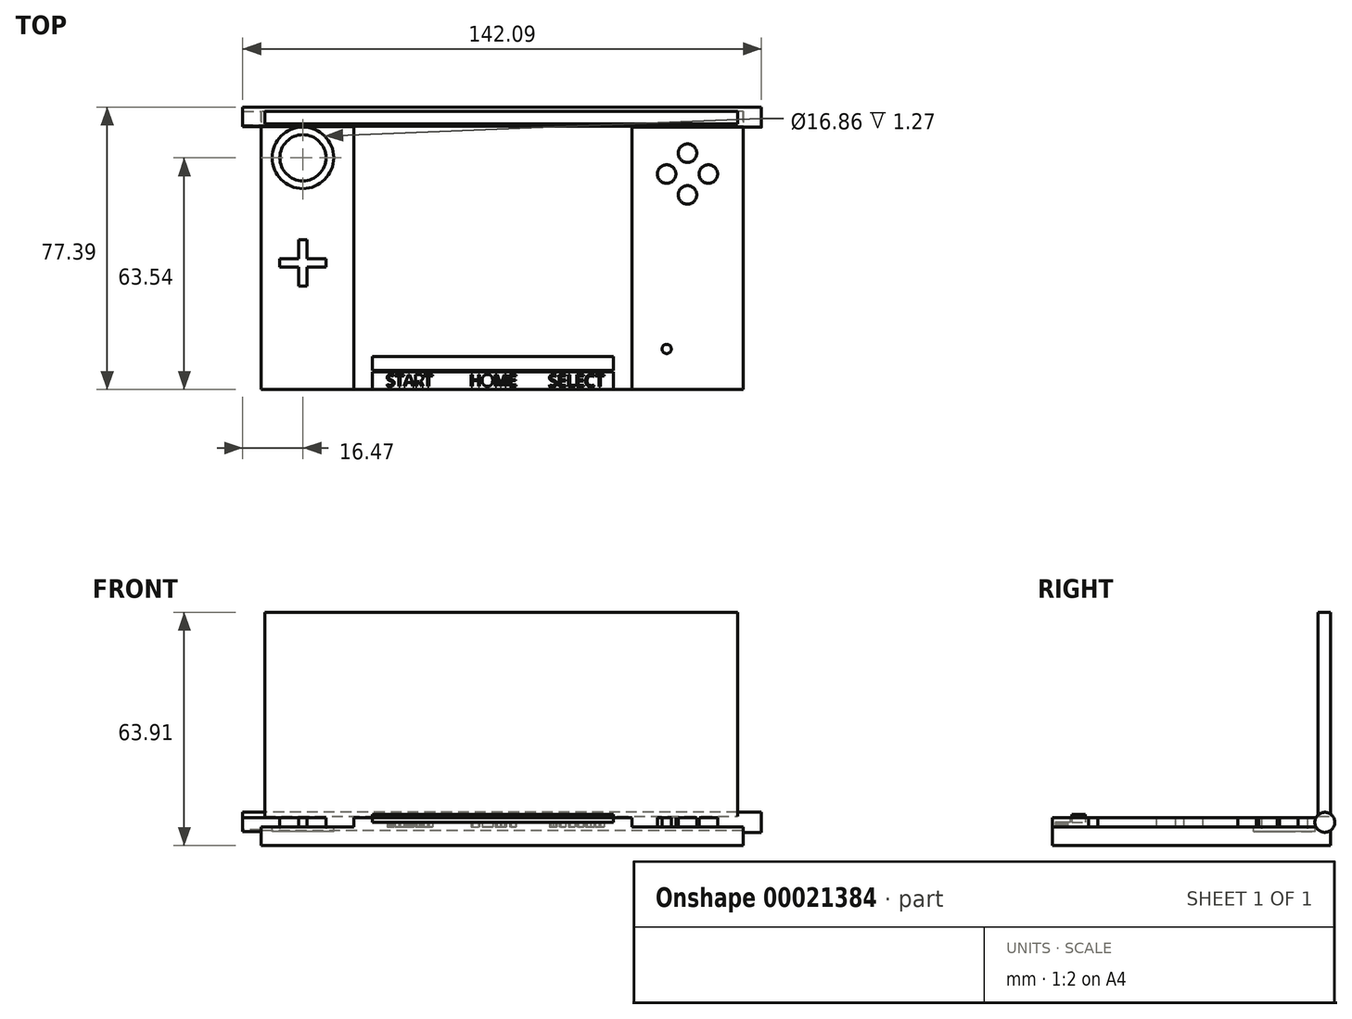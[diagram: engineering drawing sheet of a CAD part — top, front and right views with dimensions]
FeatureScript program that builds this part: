
annotation { "Feature Type Name" : "Feature", "Feature Type Description" : "" }
export const myFeature = defineFeature(function(context is Context, id is Id, definition is map)
    precondition{}
    {
        {
            var Q0;
            Q0=qCreatedBy(makeId("Front.planeOp"),FACE);
            var sketch = newSketch(context, id + "F0", { "sketchPlane" : qUnion([Q0])});
            skLineSegment(sketch, "E0.rect.bottom", {"start": v(-66.04, -2.54) * mm, "end": v(66.04, -2.54) * mm});
            skLineSegment(sketch, "E0.rect.top", {"start": v(-66.04, 2.54) * mm, "end": v(66.04, 2.54) * mm});
            skLineSegment(sketch, "E0.rect.left", {"start": v(-66.04, -2.54) * mm, "end": v(-66.04, 2.54) * mm});
            skLineSegment(sketch, "E0.rect.right", {"start": v(66.04, -2.54) * mm, "end": v(66.04, 2.54) * mm});
            skPoint(sketch, "E0.rect.middle", {"position": v(0, 0) * mm});
            skSolve(sketch);
        }
        {
            var Q0;
            Q0=makeQuery(id+"F0.imprint","IMPRINT",FACE,{"disambiguationData":[TD([[makeQuery(id+"F0.imprint","IMPRINT",EDGE,{"derivedFrom":sQuery(id+"F0.wireOp",EDGE,"E0.rect.bottom")}),1.0]])]});
            extrude(context, id + "F1", {"entities" : qUnion([Q0]), "depth" : 76.2 * mm});
        }
        {
            var Q0;
            Q0=makeQuery(id+"F1.opExtrude","SWEPT_FACE",FACE,{"disambiguationData":[OSD([sQuery(id+"F0.wireOp",EDGE,"E0.rect.top")])]});
            var sketch = newSketch(context, id + "F2", { "sketchPlane" : qUnion([Q0])});
            skLineSegment(sketch, "E1.bottom", {"start": v(-40.64, 0) * mm, "end": v(35.56, 0) * mm});
            skLineSegment(sketch, "E1.top", {"start": v(-40.64, -76.2) * mm, "end": v(35.56, -76.2) * mm});
            skLineSegment(sketch, "E1.left", {"start": v(-40.64, 0) * mm, "end": v(-40.64, -76.2) * mm});
            skLineSegment(sketch, "E1.right", {"start": v(35.56, 0) * mm, "end": v(35.56, -76.2) * mm});
            skLineSegment(sketch, "E2.bottom", {"start": v(-36.83, -71.12) * mm, "end": v(-13.97, -71.12) * mm});
            skLineSegment(sketch, "E2.top", {"start": v(-36.83, -76.2) * mm, "end": v(-13.97, -76.2) * mm});
            skLineSegment(sketch, "E2.left", {"start": v(-36.83, -71.12) * mm, "end": v(-36.83, -76.2) * mm});
            skLineSegment(sketch, "E2.right", {"start": v(-13.97, -71.12) * mm, "end": v(-13.97, -76.2) * mm});
            skLineSegment(sketch, "E3.bottom", {"start": v(31.75, -71.12) * mm, "end": v(8.9, -71.12) * mm});
            skLineSegment(sketch, "E3.top", {"start": v(31.75, -76.2) * mm, "end": v(8.9, -76.2) * mm});
            skLineSegment(sketch, "E3.left", {"start": v(31.75, -71.12) * mm, "end": v(31.75, -76.2) * mm});
            skLineSegment(sketch, "E3.right", {"start": v(8.9, -71.12) * mm, "end": v(8.9, -76.2) * mm});
            skLineSegment(sketch, "E4.bottom", {"start": v(-13.97, -71.12) * mm, "end": v(8.9, -71.12) * mm});
            skLineSegment(sketch, "E4.top", {"start": v(-13.97, -76.2) * mm, "end": v(8.9, -76.2) * mm});
            skText(sketch, "E5", { "text": "START\n", "fontName": "OpenSans-Regular.ttf"});
            skText(sketch, "E6", { "text": "HOME\n", "fontName": "OpenSans-Regular.ttf"});
            skText(sketch, "E7", { "text": "SELECT", "fontName": "OpenSans-Regular.ttf"});
            skCircle(sketch, "E8", {"center": v(-54.57, -12.66) * mm, "radius": 6.31 * mm});
            skLineSegment(sketch, "E9.rect.bottom", {"start": v(-55.71, -35.1) * mm, "end": v(-53.43, -35.1) * mm});
            skLineSegment(sketch, "E9.rect.top", {"start": v(-55.71, -47.8) * mm, "end": v(-53.43, -47.8) * mm});
            skLineSegment(sketch, "E9.rect.left", {"start": v(-55.71, -35.1) * mm, "end": v(-55.71, -47.8) * mm});
            skLineSegment(sketch, "E9.rect.right", {"start": v(-53.43, -35.1) * mm, "end": v(-53.43, -47.8) * mm});
            skPoint(sketch, "E9.rect.middle", {"position": v(-54.57, -41.45) * mm});
            skLineSegment(sketch, "E10.rect.bottom", {"start": v(-60.92, -40.3) * mm, "end": v(-48.22, -40.3) * mm});
            skLineSegment(sketch, "E10.rect.top", {"start": v(-60.92, -42.6) * mm, "end": v(-48.22, -42.6) * mm});
            skLineSegment(sketch, "E10.rect.left", {"start": v(-60.92, -40.3) * mm, "end": v(-60.92, -42.6) * mm});
            skLineSegment(sketch, "E10.rect.right", {"start": v(-48.22, -40.3) * mm, "end": v(-48.22, -42.6) * mm});
            skCircle(sketch, "E11", {"center": v(50.8, -11.4) * mm, "radius": 2.54 * mm});
            skCircle(sketch, "E12", {"center": v(50.8, -22.83) * mm, "radius": 2.54 * mm});
            skLineSegment(sketch, "E13.rect.bottom", {"start": v(49.85, -18.05) * mm, "end": v(51.75, -18.05) * mm});
            skLineSegment(sketch, "E13.rect.top", {"start": v(49.85, -16.17) * mm, "end": v(51.75, -16.17) * mm});
            skLineSegment(sketch, "E13.rect.left", {"start": v(49.85, -18.05) * mm, "end": v(49.85, -16.17) * mm});
            skLineSegment(sketch, "E13.rect.right", {"start": v(51.75, -18.05) * mm, "end": v(51.75, -16.17) * mm});
            skPoint(sketch, "E13.rect.middle", {"position": v(50.8, -17.11) * mm});
            skCircle(sketch, "E14", {"center": v(56.52, -17.11) * mm, "radius": 2.54 * mm});
            skCircle(sketch, "E15", {"center": v(45.09, -17.11) * mm, "radius": 2.54 * mm});
            skCircle(sketch, "E16", {"center": v(45.09, -65.04) * mm, "radius": 1.27 * mm});
            skCircle(sketch, "E17", {"center": v(59.7, -69.85) * mm, "radius": 6.35 * mm});
            skPoint(sketch, "E17.first.point", {"position": v(66.04, -69.85) * mm});
            skPoint(sketch, "E17.second.point", {"position": v(53.36, -70.38) * mm});
            skPoint(sketch, "E17.third.point", {"position": v(59.7, -76.2) * mm});
            skCircle(sketch, "E18", {"center": v(-59.7, -69.85) * mm, "radius": 6.35 * mm});
            skPoint(sketch, "E18.first.point", {"position": v(-59.7, -76.2) * mm});
            skPoint(sketch, "E18.second.point", {"position": v(-60.75, -63.59) * mm});
            skPoint(sketch, "E18.third.point", {"position": v(-66.04, -69.85) * mm});
            const initialGuessF2  = {"E5": [-0.03175, -0.07523, 1, 0, 0.00316], "E6": [-0.00894, -0.07523, 1, 0, 0.00315], "E7": [0.0127, -0.07536, 1, 0, 0.00327]};
            skSetInitialGuess(sketch, initialGuessF2);
            skSolve(sketch);
        }
        {
            var Q0;
            Q0=makeQuery(id+"F2.imprint","IMPRINT",FACE,{"disambiguationData":[TD([[makeQuery(id+"F2.imprint","IMPRINT",EDGE,{"derivedFrom":sQuery(id+"F2.wireOp",EDGE,"E8")}),1.0]])]});
            var Q1;
            Q1=makeQuery(id+"F2.imprint","IMPRINT",FACE,{"disambiguationData":[TD([[makeQuery(id+"F2.imprint","IMPRINT",EDGE,{"derivedFrom":sQuery(id+"F2.wireOp",EDGE,"E11")}),1.0]])]});
            var Q2;
            Q2=makeQuery(id+"F2.imprint","IMPRINT",FACE,{"disambiguationData":[TD([[makeQuery(id+"F2.imprint","IMPRINT",EDGE,{"derivedFrom":sQuery(id+"F2.wireOp",EDGE,"E12")}),1.0]])]});
            var Q3;
            Q3=makeQuery(id+"F2.imprint","IMPRINT",FACE,{"disambiguationData":[TD([[makeQuery(id+"F2.imprint","IMPRINT",EDGE,{"derivedFrom":sQuery(id+"F2.wireOp",EDGE,"E14")}),1.0]])]});
            var Q4;
            Q4=makeQuery(id+"F2.imprint","IMPRINT",FACE,{"disambiguationData":[TD([[makeQuery(id+"F2.imprint","IMPRINT",EDGE,{"derivedFrom":sQuery(id+"F2.wireOp",EDGE,"E15")}),1.0]])]});
            var Q5;
            {var subQ5=sQuery(id+"F2.wireOp",EDGE,"E9.rect.bottom");Q5=makeQuery(id+"F2.imprint","IMPRINT",FACE,{"disambiguationData":[TD([[makeQuery(id+"F2.imprint","IMPRINT",EDGE,{"derivedFrom":subQ5}),-1.0]])]});}
            var Q6;
            {var subQ5=sQuery(id+"F2.wireOp",EDGE,"E9.rect.top");Q6=makeQuery(id+"F2.imprint","IMPRINT",FACE,{"disambiguationData":[TD([[makeQuery(id+"F2.imprint","IMPRINT",EDGE,{"derivedFrom":subQ5}),1.0]])]});}
            var Q7;
            {var subQ0=sQuery(id+"F2.wireOp",EDGE,"E10.rect.left");Q7=makeQuery(id+"F2.imprint","IMPRINT",FACE,{"disambiguationData":[TD([[makeQuery(id+"F2.imprint","IMPRINT",EDGE,{"derivedFrom":subQ0}),1.0]])]});}
            var Q8;
            {var subQ0=sQuery(id+"F2.wireOp",EDGE,"E10.rect.right");Q8=makeQuery(id+"F2.imprint","IMPRINT",FACE,{"disambiguationData":[TD([[makeQuery(id+"F2.imprint","IMPRINT",EDGE,{"derivedFrom":subQ0}),-1.0]])]});}
            var Q9;
            {var subQ3=sQuery(id+"F2.wireOp",EDGE,"E9.rect.left");var subQ5=sQuery(id+"F2.wireOp",EDGE,"E10.rect.bottom");var subQ7=makeQuery(id+"F2.imprint","INTERSECT",VERTEX,{"derivedFrom":[subQ3,subQ5]});Q9=makeQuery(id+"F2.imprint","IMPRINT",FACE,{"disambiguationData":[TD([[makeQuery(id+"F2.imprint","IMPRINT",EDGE,{"disambiguationData":[TD([[subQ7,-1.0]])],"derivedFrom":subQ3}),1.0]])]});}
            var Q10;
            Q10=makeQuery(id+"F2.imprint","IMPRINT",FACE,{"disambiguationData":[TD([[makeQuery(id+"F2.imprint","IMPRINT",EDGE,{"derivedFrom":sQuery(id+"F2.wireOp",EDGE,"E1.bottom")}),-1.0]])]});
            var Q11;
            Q11=makeQuery(id+"F2.imprint","IMPRINT",FACE,{"disambiguationData":[TD([[makeQuery(id+"F2.imprint","IMPRINT",EDGE,{"derivedFrom":sQuery(id+"F2.wireOp",EDGE,"E2.bottom")}),-1.0]])]});
            var Q12;
            Q12=makeQuery(id+"F2.imprint","IMPRINT",FACE,{"disambiguationData":[TD([[makeQuery(id+"F2.imprint","IMPRINT",EDGE,{"derivedFrom":sQuery(id+"F2.wireOp",EDGE,"E4.bottom")}),-1.0]])]});
            var Q13;
            Q13=makeQuery(id+"F2.imprint","IMPRINT",FACE,{"disambiguationData":[TD([[makeQuery(id+"F2.imprint","IMPRINT",EDGE,{"derivedFrom":sQuery(id+"F2.wireOp",EDGE,"E3.bottom")}),1.0]])]});
            var Q14;
            Q14=makeQuery(id+"F2.imprint","IMPRINT",FACE,{"disambiguationData":[TD([[makeQuery(id+"F2.imprint","IMPRINT",EDGE,{"derivedFrom":sQuery(id+"F2.wireOp",EDGE,"E16")}),1.0]])]});
            extrude(context, id + "F3", {"entities" : qUnion([Q0, Q1, Q2, Q3, Q4, Q5, Q6, Q7, Q8, Q9, Q10, Q11, Q12, Q13, Q14]), "operationType" : NewBodyOperationType.ADD, "depth" : 2.54 * mm});
        }
        {
            var Q0;
            {var subQ0=sQuery(id+"F0.wireOp",EDGE,"E0.rect.top");var subQ1=sQuery(id+"F0.wireOp",EDGE,"E0.rect.left");Q0=makeQuery(id+"F3.boolean.opBoolean","SPLIT",FACE,{"disambiguationData":[TD([makeQuery(id+"F1.opExtrude","SWEPT_FACE",FACE,{"disambiguationData":[OSD([subQ1])]})])],"derivedFrom":makeQuery(id+"F1.opExtrude","SWEPT_FACE",FACE,{"disambiguationData":[OSD([subQ0])]})});}
            var sketch = newSketch(context, id + "F4", { "sketchPlane" : qUnion([Q0])});
            skCircle(sketch, "E19", {"center": v(-54.57, -12.66) * mm, "radius": 8.43 * mm});
            skSolve(sketch);
        }
        {
            var Q0;
            Q0=makeQuery(id+"F4.imprint","IMPRINT",FACE,{"disambiguationData":[TD([[makeQuery(id+"F4.imprint","IMPRINT",EDGE,{"derivedFrom":sQuery(id+"F4.wireOp",EDGE,"E19")}),1.0]])]});
            extrude(context, id + "F5", {"entities" : qUnion([Q0]), "operationType" : NewBodyOperationType.REMOVE, "oppositeDirection" : true, "depth" : 1.27 * mm});
        }
        {
            var Q0;
            Q0=qCreatedBy(makeId("Right.planeOp"),FACE);
            var sketch = newSketch(context, id + "F6", { "sketchPlane" : qUnion([Q0])});
            skCircle(sketch, "E20", {"center": v(-1.55, 3.81) * mm, "radius": 2.74 * mm});
            skSolve(sketch);
        }
        {
            var Q0;
            Q0=makeQuery(id+"F6.imprint","IMPRINT",FACE,{"disambiguationData":[TD([[makeQuery(id+"F6.imprint","IMPRINT",EDGE,{"derivedFrom":sQuery(id+"F6.wireOp",EDGE,"E20")}),1.0]])]});
            extrude(context, id + "F7", {"entities" : qUnion([Q0]), "operationType" : NewBodyOperationType.ADD, "depth" : 71.05 * mm});
        }
        {
            var Q0;
            Q0=makeQuery(id+"F7.opExtrude","CAP_FACE",FACE,{"disambiguationData":[OSD([sQuery(id+"F6.wireOp",EDGE,"E20")])],"isStart":true});
            extrude(context, id + "F8", {"entities" : qUnion([Q0]), "operationType" : NewBodyOperationType.ADD, "depth" : 71.04 * mm});
        }
        {
            var Q0;
            Q0=makeQuery(id+"F3.opExtrude","CAP_FACE",FACE,{"disambiguationData":[OSD([sQuery(id+"F2.wireOp",EDGE,"E1.bottom"),sQuery(id+"F2.wireOp",EDGE,"E1.top"),sQuery(id+"F2.wireOp",EDGE,"E1.left"),sQuery(id+"F2.wireOp",EDGE,"E1.right"),sQuery(id+"F2.wireOp",EDGE,"E2.top"),sQuery(id+"F2.wireOp",EDGE,"E3.top"),sQuery(id+"F2.wireOp",EDGE,"E4.top"),sQuery(id+"F2.wireOp",EDGE,"E5.sketch_text.stroke-0"),sQuery(id+"F2.wireOp",EDGE,"E5.sketch_text.stroke-1"),sQuery(id+"F2.wireOp",EDGE,"E5.sketch_text.stroke-2"),sQuery(id+"F2.wireOp",EDGE,"E5.sketch_text.stroke-3"),sQuery(id+"F2.wireOp",EDGE,"E5.sketch_text.stroke-4"),sQuery(id+"F2.wireOp",EDGE,"E5.sketch_text.stroke-5"),sQuery(id+"F2.wireOp",EDGE,"E5.sketch_text.stroke-6"),sQuery(id+"F2.wireOp",EDGE,"E5.sketch_text.stroke-7"),sQuery(id+"F2.wireOp",EDGE,"E5.sketch_text.stroke-8"),sQuery(id+"F2.wireOp",EDGE,"E5.sketch_text.stroke-9"),sQuery(id+"F2.wireOp",EDGE,"E5.sketch_text.stroke-10"),sQuery(id+"F2.wireOp",EDGE,"E5.sketch_text.stroke-11"),sQuery(id+"F2.wireOp",EDGE,"E5.sketch_text.stroke-12"),sQuery(id+"F2.wireOp",EDGE,"E5.sketch_text.stroke-13"),sQuery(id+"F2.wireOp",EDGE,"E5.sketch_text.stroke-14"),sQuery(id+"F2.wireOp",EDGE,"E5.sketch_text.stroke-15"),sQuery(id+"F2.wireOp",EDGE,"E5.sketch_text.stroke-16"),sQuery(id+"F2.wireOp",EDGE,"E5.sketch_text.stroke-17"),sQuery(id+"F2.wireOp",EDGE,"E5.sketch_text.stroke-18"),sQuery(id+"F2.wireOp",EDGE,"E5.sketch_text.stroke-19"),sQuery(id+"F2.wireOp",EDGE,"E5.sketch_text.stroke-20"),sQuery(id+"F2.wireOp",EDGE,"E5.sketch_text.stroke-21"),sQuery(id+"F2.wireOp",EDGE,"E5.sketch_text.stroke-22"),sQuery(id+"F2.wireOp",EDGE,"E5.sketch_text.stroke-23"),sQuery(id+"F2.wireOp",EDGE,"E5.sketch_text.stroke-24"),sQuery(id+"F2.wireOp",EDGE,"E5.sketch_text.stroke-25"),sQuery(id+"F2.wireOp",EDGE,"E5.sketch_text.stroke-26"),sQuery(id+"F2.wireOp",EDGE,"E5.sketch_text.stroke-27"),sQuery(id+"F2.wireOp",EDGE,"E5.sketch_text.stroke-28"),sQuery(id+"F2.wireOp",EDGE,"E5.sketch_text.stroke-29"),sQuery(id+"F2.wireOp",EDGE,"E5.sketch_text.stroke-30"),sQuery(id+"F2.wireOp",EDGE,"E5.sketch_text.stroke-31"),sQuery(id+"F2.wireOp",EDGE,"E5.sketch_text.stroke-32"),sQuery(id+"F2.wireOp",EDGE,"E5.sketch_text.stroke-33"),sQuery(id+"F2.wireOp",EDGE,"E5.sketch_text.stroke-34"),sQuery(id+"F2.wireOp",EDGE,"E5.sketch_text.stroke-35"),sQuery(id+"F2.wireOp",EDGE,"E5.sketch_text.stroke-36"),sQuery(id+"F2.wireOp",EDGE,"E5.sketch_text.stroke-37"),sQuery(id+"F2.wireOp",EDGE,"E5.sketch_text.stroke-38"),sQuery(id+"F2.wireOp",EDGE,"E5.sketch_text.stroke-39"),sQuery(id+"F2.wireOp",EDGE,"E5.sketch_text.stroke-40"),sQuery(id+"F2.wireOp",EDGE,"E5.sketch_text.stroke-46"),sQuery(id+"F2.wireOp",EDGE,"E5.sketch_text.stroke-47"),sQuery(id+"F2.wireOp",EDGE,"E5.sketch_text.stroke-48"),sQuery(id+"F2.wireOp",EDGE,"E5.sketch_text.stroke-49"),sQuery(id+"F2.wireOp",EDGE,"E5.sketch_text.stroke-50"),sQuery(id+"F2.wireOp",EDGE,"E5.sketch_text.stroke-51"),sQuery(id+"F2.wireOp",EDGE,"E5.sketch_text.stroke-52"),sQuery(id+"F2.wireOp",EDGE,"E5.sketch_text.stroke-53"),sQuery(id+"F2.wireOp",EDGE,"E5.sketch_text.stroke-54"),sQuery(id+"F2.wireOp",EDGE,"E5.sketch_text.stroke-55"),sQuery(id+"F2.wireOp",EDGE,"E5.sketch_text.stroke-56"),sQuery(id+"F2.wireOp",EDGE,"E5.sketch_text.stroke-64"),sQuery(id+"F2.wireOp",EDGE,"E5.sketch_text.stroke-65"),sQuery(id+"F2.wireOp",EDGE,"E5.sketch_text.stroke-66"),sQuery(id+"F2.wireOp",EDGE,"E5.sketch_text.stroke-67"),sQuery(id+"F2.wireOp",EDGE,"E5.sketch_text.stroke-68"),sQuery(id+"F2.wireOp",EDGE,"E5.sketch_text.stroke-69"),sQuery(id+"F2.wireOp",EDGE,"E5.sketch_text.stroke-70"),sQuery(id+"F2.wireOp",EDGE,"E5.sketch_text.stroke-71"),sQuery(id+"F2.wireOp",EDGE,"E6.sketch_text.stroke-0"),sQuery(id+"F2.wireOp",EDGE,"E6.sketch_text.stroke-1"),sQuery(id+"F2.wireOp",EDGE,"E6.sketch_text.stroke-2"),sQuery(id+"F2.wireOp",EDGE,"E6.sketch_text.stroke-3"),sQuery(id+"F2.wireOp",EDGE,"E6.sketch_text.stroke-4"),sQuery(id+"F2.wireOp",EDGE,"E6.sketch_text.stroke-5"),sQuery(id+"F2.wireOp",EDGE,"E6.sketch_text.stroke-6"),sQuery(id+"F2.wireOp",EDGE,"E6.sketch_text.stroke-7"),sQuery(id+"F2.wireOp",EDGE,"E6.sketch_text.stroke-8"),sQuery(id+"F2.wireOp",EDGE,"E6.sketch_text.stroke-9"),sQuery(id+"F2.wireOp",EDGE,"E6.sketch_text.stroke-10"),sQuery(id+"F2.wireOp",EDGE,"E6.sketch_text.stroke-11"),sQuery(id+"F2.wireOp",EDGE,"E6.sketch_text.stroke-12"),sQuery(id+"F2.wireOp",EDGE,"E6.sketch_text.stroke-13"),sQuery(id+"F2.wireOp",EDGE,"E6.sketch_text.stroke-14"),sQuery(id+"F2.wireOp",EDGE,"E6.sketch_text.stroke-15"),sQuery(id+"F2.wireOp",EDGE,"E6.sketch_text.stroke-16"),sQuery(id+"F2.wireOp",EDGE,"E6.sketch_text.stroke-17"),sQuery(id+"F2.wireOp",EDGE,"E6.sketch_text.stroke-18"),sQuery(id+"F2.wireOp",EDGE,"E6.sketch_text.stroke-19"),sQuery(id+"F2.wireOp",EDGE,"E6.sketch_text.stroke-28"),sQuery(id+"F2.wireOp",EDGE,"E6.sketch_text.stroke-29"),sQuery(id+"F2.wireOp",EDGE,"E6.sketch_text.stroke-30"),sQuery(id+"F2.wireOp",EDGE,"E6.sketch_text.stroke-31"),sQuery(id+"F2.wireOp",EDGE,"E6.sketch_text.stroke-32"),sQuery(id+"F2.wireOp",EDGE,"E6.sketch_text.stroke-33"),sQuery(id+"F2.wireOp",EDGE,"E6.sketch_text.stroke-34"),sQuery(id+"F2.wireOp",EDGE,"E6.sketch_text.stroke-35"),sQuery(id+"F2.wireOp",EDGE,"E6.sketch_text.stroke-36"),sQuery(id+"F2.wireOp",EDGE,"E6.sketch_text.stroke-37"),sQuery(id+"F2.wireOp",EDGE,"E6.sketch_text.stroke-38"),sQuery(id+"F2.wireOp",EDGE,"E6.sketch_text.stroke-39"),sQuery(id+"F2.wireOp",EDGE,"E6.sketch_text.stroke-40"),sQuery(id+"F2.wireOp",EDGE,"E6.sketch_text.stroke-41"),sQuery(id+"F2.wireOp",EDGE,"E6.sketch_text.stroke-42"),sQuery(id+"F2.wireOp",EDGE,"E6.sketch_text.stroke-43"),sQuery(id+"F2.wireOp",EDGE,"E6.sketch_text.stroke-44"),sQuery(id+"F2.wireOp",EDGE,"E6.sketch_text.stroke-45"),sQuery(id+"F2.wireOp",EDGE,"E6.sketch_text.stroke-46"),sQuery(id+"F2.wireOp",EDGE,"E6.sketch_text.stroke-47"),sQuery(id+"F2.wireOp",EDGE,"E6.sketch_text.stroke-48"),sQuery(id+"F2.wireOp",EDGE,"E6.sketch_text.stroke-49"),sQuery(id+"F2.wireOp",EDGE,"E6.sketch_text.stroke-50"),sQuery(id+"F2.wireOp",EDGE,"E6.sketch_text.stroke-51"),sQuery(id+"F2.wireOp",EDGE,"E6.sketch_text.stroke-52"),sQuery(id+"F2.wireOp",EDGE,"E6.sketch_text.stroke-53"),sQuery(id+"F2.wireOp",EDGE,"E6.sketch_text.stroke-54"),sQuery(id+"F2.wireOp",EDGE,"E6.sketch_text.stroke-55"),sQuery(id+"F2.wireOp",EDGE,"E6.sketch_text.stroke-56"),sQuery(id+"F2.wireOp",EDGE,"E6.sketch_text.stroke-57"),sQuery(id+"F2.wireOp",EDGE,"E7.sketch_text.stroke-0"),sQuery(id+"F2.wireOp",EDGE,"E7.sketch_text.stroke-1"),sQuery(id+"F2.wireOp",EDGE,"E7.sketch_text.stroke-2"),sQuery(id+"F2.wireOp",EDGE,"E7.sketch_text.stroke-3"),sQuery(id+"F2.wireOp",EDGE,"E7.sketch_text.stroke-4"),sQuery(id+"F2.wireOp",EDGE,"E7.sketch_text.stroke-5"),sQuery(id+"F2.wireOp",EDGE,"E7.sketch_text.stroke-6"),sQuery(id+"F2.wireOp",EDGE,"E7.sketch_text.stroke-7"),sQuery(id+"F2.wireOp",EDGE,"E7.sketch_text.stroke-8"),sQuery(id+"F2.wireOp",EDGE,"E7.sketch_text.stroke-9"),sQuery(id+"F2.wireOp",EDGE,"E7.sketch_text.stroke-10"),sQuery(id+"F2.wireOp",EDGE,"E7.sketch_text.stroke-11"),sQuery(id+"F2.wireOp",EDGE,"E7.sketch_text.stroke-12"),sQuery(id+"F2.wireOp",EDGE,"E7.sketch_text.stroke-13"),sQuery(id+"F2.wireOp",EDGE,"E7.sketch_text.stroke-14"),sQuery(id+"F2.wireOp",EDGE,"E7.sketch_text.stroke-15"),sQuery(id+"F2.wireOp",EDGE,"E7.sketch_text.stroke-16"),sQuery(id+"F2.wireOp",EDGE,"E7.sketch_text.stroke-17"),sQuery(id+"F2.wireOp",EDGE,"E7.sketch_text.stroke-18"),sQuery(id+"F2.wireOp",EDGE,"E7.sketch_text.stroke-19"),sQuery(id+"F2.wireOp",EDGE,"E7.sketch_text.stroke-20"),sQuery(id+"F2.wireOp",EDGE,"E7.sketch_text.stroke-21"),sQuery(id+"F2.wireOp",EDGE,"E7.sketch_text.stroke-22"),sQuery(id+"F2.wireOp",EDGE,"E7.sketch_text.stroke-23"),sQuery(id+"F2.wireOp",EDGE,"E7.sketch_text.stroke-24"),sQuery(id+"F2.wireOp",EDGE,"E7.sketch_text.stroke-25"),sQuery(id+"F2.wireOp",EDGE,"E7.sketch_text.stroke-26"),sQuery(id+"F2.wireOp",EDGE,"E7.sketch_text.stroke-27"),sQuery(id+"F2.wireOp",EDGE,"E7.sketch_text.stroke-28"),sQuery(id+"F2.wireOp",EDGE,"E7.sketch_text.stroke-29"),sQuery(id+"F2.wireOp",EDGE,"E7.sketch_text.stroke-30"),sQuery(id+"F2.wireOp",EDGE,"E7.sketch_text.stroke-31"),sQuery(id+"F2.wireOp",EDGE,"E7.sketch_text.stroke-32"),sQuery(id+"F2.wireOp",EDGE,"E7.sketch_text.stroke-33"),sQuery(id+"F2.wireOp",EDGE,"E7.sketch_text.stroke-34"),sQuery(id+"F2.wireOp",EDGE,"E7.sketch_text.stroke-35"),sQuery(id+"F2.wireOp",EDGE,"E7.sketch_text.stroke-36"),sQuery(id+"F2.wireOp",EDGE,"E7.sketch_text.stroke-37"),sQuery(id+"F2.wireOp",EDGE,"E7.sketch_text.stroke-38"),sQuery(id+"F2.wireOp",EDGE,"E7.sketch_text.stroke-39"),sQuery(id+"F2.wireOp",EDGE,"E7.sketch_text.stroke-40"),sQuery(id+"F2.wireOp",EDGE,"E7.sketch_text.stroke-41"),sQuery(id+"F2.wireOp",EDGE,"E7.sketch_text.stroke-42"),sQuery(id+"F2.wireOp",EDGE,"E7.sketch_text.stroke-43"),sQuery(id+"F2.wireOp",EDGE,"E7.sketch_text.stroke-44"),sQuery(id+"F2.wireOp",EDGE,"E7.sketch_text.stroke-45"),sQuery(id+"F2.wireOp",EDGE,"E7.sketch_text.stroke-46"),sQuery(id+"F2.wireOp",EDGE,"E7.sketch_text.stroke-47"),sQuery(id+"F2.wireOp",EDGE,"E7.sketch_text.stroke-48"),sQuery(id+"F2.wireOp",EDGE,"E7.sketch_text.stroke-49"),sQuery(id+"F2.wireOp",EDGE,"E7.sketch_text.stroke-50"),sQuery(id+"F2.wireOp",EDGE,"E7.sketch_text.stroke-51"),sQuery(id+"F2.wireOp",EDGE,"E7.sketch_text.stroke-52"),sQuery(id+"F2.wireOp",EDGE,"E7.sketch_text.stroke-53"),sQuery(id+"F2.wireOp",EDGE,"E7.sketch_text.stroke-54"),sQuery(id+"F2.wireOp",EDGE,"E7.sketch_text.stroke-55"),sQuery(id+"F2.wireOp",EDGE,"E7.sketch_text.stroke-56"),sQuery(id+"F2.wireOp",EDGE,"E7.sketch_text.stroke-57"),sQuery(id+"F2.wireOp",EDGE,"E7.sketch_text.stroke-58"),sQuery(id+"F2.wireOp",EDGE,"E7.sketch_text.stroke-59"),sQuery(id+"F2.wireOp",EDGE,"E7.sketch_text.stroke-60"),sQuery(id+"F2.wireOp",EDGE,"E7.sketch_text.stroke-61"),sQuery(id+"F2.wireOp",EDGE,"E7.sketch_text.stroke-62"),sQuery(id+"F2.wireOp",EDGE,"E7.sketch_text.stroke-63"),sQuery(id+"F2.wireOp",EDGE,"E7.sketch_text.stroke-64"),sQuery(id+"F2.wireOp",EDGE,"E7.sketch_text.stroke-65"),sQuery(id+"F2.wireOp",EDGE,"E7.sketch_text.stroke-66"),sQuery(id+"F2.wireOp",EDGE,"E7.sketch_text.stroke-67"),sQuery(id+"F2.wireOp",EDGE,"E7.sketch_text.stroke-68"),sQuery(id+"F2.wireOp",EDGE,"E7.sketch_text.stroke-69"),sQuery(id+"F2.wireOp",EDGE,"E7.sketch_text.stroke-70"),sQuery(id+"F2.wireOp",EDGE,"E7.sketch_text.stroke-71"),sQuery(id+"F2.wireOp",EDGE,"E7.sketch_text.stroke-72"),sQuery(id+"F2.wireOp",EDGE,"E7.sketch_text.stroke-73"),sQuery(id+"F2.wireOp",EDGE,"E7.sketch_text.stroke-74"),sQuery(id+"F2.wireOp",EDGE,"E7.sketch_text.stroke-75"),sQuery(id+"F2.wireOp",EDGE,"E7.sketch_text.stroke-76"),sQuery(id+"F2.wireOp",EDGE,"E7.sketch_text.stroke-77")])],"isStart":false});
            var sketch = newSketch(context, id + "F9", { "sketchPlane" : qUnion([Q0])});
            skLineSegment(sketch, "E21.rect.bottom", {"start": v(-35.56, -2.7) * mm, "end": v(30.48, -2.7) * mm});
            skLineSegment(sketch, "E21.rect.top", {"start": v(-35.56, -71.29) * mm, "end": v(30.48, -71.29) * mm});
            skLineSegment(sketch, "E21.rect.left", {"start": v(-35.56, -2.7) * mm, "end": v(-35.56, -71.29) * mm});
            skLineSegment(sketch, "E21.rect.right", {"start": v(30.48, -2.7) * mm, "end": v(30.48, -71.29) * mm});
            skPoint(sketch, "E21.rect.middle", {"position": v(-2.54, -37) * mm});
            skLineSegment(sketch, "E22", {"start": v(-35.56, -71.29) * mm, "end": v(-35.56, -76.2) * mm});
            skLineSegment(sketch, "E23", {"start": v(-35.56, -76.2) * mm, "end": v(30.48, -76.2) * mm});
            skLineSegment(sketch, "E24", {"start": v(30.48, -76.2) * mm, "end": v(30.48, -71.29) * mm});
            skLineSegment(sketch, "E25", {"start": v(8.69, -71.29) * mm, "end": v(8.69, -76.2) * mm});
            skLineSegment(sketch, "E26", {"start": v(8.69, -76.2) * mm, "end": v(-13.77, -76.2) * mm});
            skLineSegment(sketch, "E27", {"start": v(-13.77, -76.2) * mm, "end": v(-13.77, -71.29) * mm});
            skLineSegment(sketch, "E28", {"start": v(-13.77, -71.29) * mm, "end": v(8.69, -71.29) * mm});
            skSolve(sketch);
        }
        {
            var Q0;
            {var subQ201=sQuery(id+"F9.wireOp",EDGE,"E28");Q0=makeQuery(id+"F9.imprint","IMPRINT",FACE,{"disambiguationData":[TD([[makeQuery(id+"F9.imprint","IMPRINT",EDGE,{"derivedFrom":subQ201}),1.0]])]});}
            var Q1;
            Q1=makeQuery(id+"F9.imprint","IMPRINT",FACE,{"disambiguationData":[TD([[makeQuery(id+"F9.imprint","IMPRINT",EDGE,{"derivedFrom":sQuery(id+"F9.wireOp",EDGE,"E25")}),-1.0]])]});
            var Q2;
            {var subQ0=sQuery(id+"F9.wireOp",EDGE,"E24");Q2=makeQuery(id+"F9.imprint","IMPRINT",FACE,{"disambiguationData":[TD([[makeQuery(id+"F9.imprint","IMPRINT",EDGE,{"derivedFrom":subQ0}),1.0]])]});}
            var Q3;
            {var subQ2=sQuery(id+"F9.wireOp",EDGE,"E22");Q3=makeQuery(id+"F9.imprint","IMPRINT",FACE,{"disambiguationData":[TD([[makeQuery(id+"F9.imprint","IMPRINT",EDGE,{"derivedFrom":subQ2}),1.0]])]});}
            extrude(context, id + "F10", {"entities" : qUnion([Q0, Q1, Q2, Q3]), "operationType" : NewBodyOperationType.REMOVE, "oppositeDirection" : true, "depth" : 1.27 * mm});
        }
        {
            var Q0;
            Q0=makeQuery(id+"F10.boolean.opBoolean","COPY",FACE,{"derivedFrom":makeQuery(id+"F10.opExtrude","CAP_FACE",FACE,{"disambiguationData":[OSD([sQuery(id+"F2.wireOp",EDGE,"E1.bottom"),sQuery(id+"F2.wireOp",EDGE,"E1.top"),sQuery(id+"F2.wireOp",EDGE,"E1.left"),sQuery(id+"F2.wireOp",EDGE,"E1.right"),sQuery(id+"F2.wireOp",EDGE,"E2.top"),sQuery(id+"F2.wireOp",EDGE,"E3.top"),sQuery(id+"F2.wireOp",EDGE,"E4.top"),sQuery(id+"F2.wireOp",EDGE,"E5.sketch_text.stroke-0"),sQuery(id+"F2.wireOp",EDGE,"E5.sketch_text.stroke-1"),sQuery(id+"F2.wireOp",EDGE,"E5.sketch_text.stroke-2"),sQuery(id+"F2.wireOp",EDGE,"E5.sketch_text.stroke-3"),sQuery(id+"F2.wireOp",EDGE,"E5.sketch_text.stroke-4"),sQuery(id+"F2.wireOp",EDGE,"E5.sketch_text.stroke-5"),sQuery(id+"F2.wireOp",EDGE,"E5.sketch_text.stroke-6"),sQuery(id+"F2.wireOp",EDGE,"E5.sketch_text.stroke-7"),sQuery(id+"F2.wireOp",EDGE,"E5.sketch_text.stroke-8"),sQuery(id+"F2.wireOp",EDGE,"E5.sketch_text.stroke-9"),sQuery(id+"F2.wireOp",EDGE,"E5.sketch_text.stroke-10"),sQuery(id+"F2.wireOp",EDGE,"E5.sketch_text.stroke-11"),sQuery(id+"F2.wireOp",EDGE,"E5.sketch_text.stroke-12"),sQuery(id+"F2.wireOp",EDGE,"E5.sketch_text.stroke-13"),sQuery(id+"F2.wireOp",EDGE,"E5.sketch_text.stroke-14"),sQuery(id+"F2.wireOp",EDGE,"E5.sketch_text.stroke-15"),sQuery(id+"F2.wireOp",EDGE,"E5.sketch_text.stroke-16"),sQuery(id+"F2.wireOp",EDGE,"E5.sketch_text.stroke-17"),sQuery(id+"F2.wireOp",EDGE,"E5.sketch_text.stroke-18"),sQuery(id+"F2.wireOp",EDGE,"E5.sketch_text.stroke-19"),sQuery(id+"F2.wireOp",EDGE,"E5.sketch_text.stroke-20"),sQuery(id+"F2.wireOp",EDGE,"E5.sketch_text.stroke-21"),sQuery(id+"F2.wireOp",EDGE,"E5.sketch_text.stroke-22"),sQuery(id+"F2.wireOp",EDGE,"E5.sketch_text.stroke-23"),sQuery(id+"F2.wireOp",EDGE,"E5.sketch_text.stroke-24"),sQuery(id+"F2.wireOp",EDGE,"E5.sketch_text.stroke-25"),sQuery(id+"F2.wireOp",EDGE,"E5.sketch_text.stroke-26"),sQuery(id+"F2.wireOp",EDGE,"E5.sketch_text.stroke-27"),sQuery(id+"F2.wireOp",EDGE,"E5.sketch_text.stroke-28"),sQuery(id+"F2.wireOp",EDGE,"E5.sketch_text.stroke-29"),sQuery(id+"F2.wireOp",EDGE,"E5.sketch_text.stroke-30"),sQuery(id+"F2.wireOp",EDGE,"E5.sketch_text.stroke-31"),sQuery(id+"F2.wireOp",EDGE,"E5.sketch_text.stroke-32"),sQuery(id+"F2.wireOp",EDGE,"E5.sketch_text.stroke-33"),sQuery(id+"F2.wireOp",EDGE,"E5.sketch_text.stroke-34"),sQuery(id+"F2.wireOp",EDGE,"E5.sketch_text.stroke-35"),sQuery(id+"F2.wireOp",EDGE,"E5.sketch_text.stroke-36"),sQuery(id+"F2.wireOp",EDGE,"E5.sketch_text.stroke-37"),sQuery(id+"F2.wireOp",EDGE,"E5.sketch_text.stroke-38"),sQuery(id+"F2.wireOp",EDGE,"E5.sketch_text.stroke-39"),sQuery(id+"F2.wireOp",EDGE,"E5.sketch_text.stroke-40"),sQuery(id+"F2.wireOp",EDGE,"E5.sketch_text.stroke-46"),sQuery(id+"F2.wireOp",EDGE,"E5.sketch_text.stroke-47"),sQuery(id+"F2.wireOp",EDGE,"E5.sketch_text.stroke-48"),sQuery(id+"F2.wireOp",EDGE,"E5.sketch_text.stroke-49"),sQuery(id+"F2.wireOp",EDGE,"E5.sketch_text.stroke-50"),sQuery(id+"F2.wireOp",EDGE,"E5.sketch_text.stroke-51"),sQuery(id+"F2.wireOp",EDGE,"E5.sketch_text.stroke-52"),sQuery(id+"F2.wireOp",EDGE,"E5.sketch_text.stroke-53"),sQuery(id+"F2.wireOp",EDGE,"E5.sketch_text.stroke-54"),sQuery(id+"F2.wireOp",EDGE,"E5.sketch_text.stroke-55"),sQuery(id+"F2.wireOp",EDGE,"E5.sketch_text.stroke-56"),sQuery(id+"F2.wireOp",EDGE,"E5.sketch_text.stroke-64"),sQuery(id+"F2.wireOp",EDGE,"E5.sketch_text.stroke-65"),sQuery(id+"F2.wireOp",EDGE,"E5.sketch_text.stroke-66"),sQuery(id+"F2.wireOp",EDGE,"E5.sketch_text.stroke-67"),sQuery(id+"F2.wireOp",EDGE,"E5.sketch_text.stroke-68"),sQuery(id+"F2.wireOp",EDGE,"E5.sketch_text.stroke-69"),sQuery(id+"F2.wireOp",EDGE,"E5.sketch_text.stroke-70"),sQuery(id+"F2.wireOp",EDGE,"E5.sketch_text.stroke-71"),sQuery(id+"F2.wireOp",EDGE,"E6.sketch_text.stroke-0"),sQuery(id+"F2.wireOp",EDGE,"E6.sketch_text.stroke-1"),sQuery(id+"F2.wireOp",EDGE,"E6.sketch_text.stroke-2"),sQuery(id+"F2.wireOp",EDGE,"E6.sketch_text.stroke-3"),sQuery(id+"F2.wireOp",EDGE,"E6.sketch_text.stroke-4"),sQuery(id+"F2.wireOp",EDGE,"E6.sketch_text.stroke-5"),sQuery(id+"F2.wireOp",EDGE,"E6.sketch_text.stroke-6"),sQuery(id+"F2.wireOp",EDGE,"E6.sketch_text.stroke-7"),sQuery(id+"F2.wireOp",EDGE,"E6.sketch_text.stroke-8"),sQuery(id+"F2.wireOp",EDGE,"E6.sketch_text.stroke-9"),sQuery(id+"F2.wireOp",EDGE,"E6.sketch_text.stroke-10"),sQuery(id+"F2.wireOp",EDGE,"E6.sketch_text.stroke-11"),sQuery(id+"F2.wireOp",EDGE,"E6.sketch_text.stroke-12"),sQuery(id+"F2.wireOp",EDGE,"E6.sketch_text.stroke-13"),sQuery(id+"F2.wireOp",EDGE,"E6.sketch_text.stroke-14"),sQuery(id+"F2.wireOp",EDGE,"E6.sketch_text.stroke-15"),sQuery(id+"F2.wireOp",EDGE,"E6.sketch_text.stroke-16"),sQuery(id+"F2.wireOp",EDGE,"E6.sketch_text.stroke-17"),sQuery(id+"F2.wireOp",EDGE,"E6.sketch_text.stroke-18"),sQuery(id+"F2.wireOp",EDGE,"E6.sketch_text.stroke-19"),sQuery(id+"F2.wireOp",EDGE,"E6.sketch_text.stroke-28"),sQuery(id+"F2.wireOp",EDGE,"E6.sketch_text.stroke-29"),sQuery(id+"F2.wireOp",EDGE,"E6.sketch_text.stroke-30"),sQuery(id+"F2.wireOp",EDGE,"E6.sketch_text.stroke-31"),sQuery(id+"F2.wireOp",EDGE,"E6.sketch_text.stroke-32"),sQuery(id+"F2.wireOp",EDGE,"E6.sketch_text.stroke-33"),sQuery(id+"F2.wireOp",EDGE,"E6.sketch_text.stroke-34"),sQuery(id+"F2.wireOp",EDGE,"E6.sketch_text.stroke-35"),sQuery(id+"F2.wireOp",EDGE,"E6.sketch_text.stroke-36"),sQuery(id+"F2.wireOp",EDGE,"E6.sketch_text.stroke-37"),sQuery(id+"F2.wireOp",EDGE,"E6.sketch_text.stroke-38"),sQuery(id+"F2.wireOp",EDGE,"E6.sketch_text.stroke-39"),sQuery(id+"F2.wireOp",EDGE,"E6.sketch_text.stroke-40"),sQuery(id+"F2.wireOp",EDGE,"E6.sketch_text.stroke-41"),sQuery(id+"F2.wireOp",EDGE,"E6.sketch_text.stroke-42"),sQuery(id+"F2.wireOp",EDGE,"E6.sketch_text.stroke-43"),sQuery(id+"F2.wireOp",EDGE,"E6.sketch_text.stroke-44"),sQuery(id+"F2.wireOp",EDGE,"E6.sketch_text.stroke-45"),sQuery(id+"F2.wireOp",EDGE,"E6.sketch_text.stroke-46"),sQuery(id+"F2.wireOp",EDGE,"E6.sketch_text.stroke-47"),sQuery(id+"F2.wireOp",EDGE,"E6.sketch_text.stroke-48"),sQuery(id+"F2.wireOp",EDGE,"E6.sketch_text.stroke-49"),sQuery(id+"F2.wireOp",EDGE,"E6.sketch_text.stroke-50"),sQuery(id+"F2.wireOp",EDGE,"E6.sketch_text.stroke-51"),sQuery(id+"F2.wireOp",EDGE,"E6.sketch_text.stroke-52"),sQuery(id+"F2.wireOp",EDGE,"E6.sketch_text.stroke-53"),sQuery(id+"F2.wireOp",EDGE,"E6.sketch_text.stroke-54"),sQuery(id+"F2.wireOp",EDGE,"E6.sketch_text.stroke-55"),sQuery(id+"F2.wireOp",EDGE,"E6.sketch_text.stroke-56"),sQuery(id+"F2.wireOp",EDGE,"E6.sketch_text.stroke-57"),sQuery(id+"F2.wireOp",EDGE,"E7.sketch_text.stroke-0"),sQuery(id+"F2.wireOp",EDGE,"E7.sketch_text.stroke-1"),sQuery(id+"F2.wireOp",EDGE,"E7.sketch_text.stroke-2"),sQuery(id+"F2.wireOp",EDGE,"E7.sketch_text.stroke-3"),sQuery(id+"F2.wireOp",EDGE,"E7.sketch_text.stroke-4"),sQuery(id+"F2.wireOp",EDGE,"E7.sketch_text.stroke-5"),sQuery(id+"F2.wireOp",EDGE,"E7.sketch_text.stroke-6"),sQuery(id+"F2.wireOp",EDGE,"E7.sketch_text.stroke-7"),sQuery(id+"F2.wireOp",EDGE,"E7.sketch_text.stroke-8"),sQuery(id+"F2.wireOp",EDGE,"E7.sketch_text.stroke-9"),sQuery(id+"F2.wireOp",EDGE,"E7.sketch_text.stroke-10"),sQuery(id+"F2.wireOp",EDGE,"E7.sketch_text.stroke-11"),sQuery(id+"F2.wireOp",EDGE,"E7.sketch_text.stroke-12"),sQuery(id+"F2.wireOp",EDGE,"E7.sketch_text.stroke-13"),sQuery(id+"F2.wireOp",EDGE,"E7.sketch_text.stroke-14"),sQuery(id+"F2.wireOp",EDGE,"E7.sketch_text.stroke-15"),sQuery(id+"F2.wireOp",EDGE,"E7.sketch_text.stroke-16"),sQuery(id+"F2.wireOp",EDGE,"E7.sketch_text.stroke-17"),sQuery(id+"F2.wireOp",EDGE,"E7.sketch_text.stroke-18"),sQuery(id+"F2.wireOp",EDGE,"E7.sketch_text.stroke-19"),sQuery(id+"F2.wireOp",EDGE,"E7.sketch_text.stroke-20"),sQuery(id+"F2.wireOp",EDGE,"E7.sketch_text.stroke-21"),sQuery(id+"F2.wireOp",EDGE,"E7.sketch_text.stroke-22"),sQuery(id+"F2.wireOp",EDGE,"E7.sketch_text.stroke-23"),sQuery(id+"F2.wireOp",EDGE,"E7.sketch_text.stroke-24"),sQuery(id+"F2.wireOp",EDGE,"E7.sketch_text.stroke-25"),sQuery(id+"F2.wireOp",EDGE,"E7.sketch_text.stroke-26"),sQuery(id+"F2.wireOp",EDGE,"E7.sketch_text.stroke-27"),sQuery(id+"F2.wireOp",EDGE,"E7.sketch_text.stroke-28"),sQuery(id+"F2.wireOp",EDGE,"E7.sketch_text.stroke-29"),sQuery(id+"F2.wireOp",EDGE,"E7.sketch_text.stroke-30"),sQuery(id+"F2.wireOp",EDGE,"E7.sketch_text.stroke-31"),sQuery(id+"F2.wireOp",EDGE,"E7.sketch_text.stroke-32"),sQuery(id+"F2.wireOp",EDGE,"E7.sketch_text.stroke-33"),sQuery(id+"F2.wireOp",EDGE,"E7.sketch_text.stroke-34"),sQuery(id+"F2.wireOp",EDGE,"E7.sketch_text.stroke-35"),sQuery(id+"F2.wireOp",EDGE,"E7.sketch_text.stroke-36"),sQuery(id+"F2.wireOp",EDGE,"E7.sketch_text.stroke-37"),sQuery(id+"F2.wireOp",EDGE,"E7.sketch_text.stroke-38"),sQuery(id+"F2.wireOp",EDGE,"E7.sketch_text.stroke-39"),sQuery(id+"F2.wireOp",EDGE,"E7.sketch_text.stroke-40"),sQuery(id+"F2.wireOp",EDGE,"E7.sketch_text.stroke-41"),sQuery(id+"F2.wireOp",EDGE,"E7.sketch_text.stroke-42"),sQuery(id+"F2.wireOp",EDGE,"E7.sketch_text.stroke-43"),sQuery(id+"F2.wireOp",EDGE,"E7.sketch_text.stroke-44"),sQuery(id+"F2.wireOp",EDGE,"E7.sketch_text.stroke-45"),sQuery(id+"F2.wireOp",EDGE,"E7.sketch_text.stroke-46"),sQuery(id+"F2.wireOp",EDGE,"E7.sketch_text.stroke-47"),sQuery(id+"F2.wireOp",EDGE,"E7.sketch_text.stroke-48"),sQuery(id+"F2.wireOp",EDGE,"E7.sketch_text.stroke-49"),sQuery(id+"F2.wireOp",EDGE,"E7.sketch_text.stroke-50"),sQuery(id+"F2.wireOp",EDGE,"E7.sketch_text.stroke-51"),sQuery(id+"F2.wireOp",EDGE,"E7.sketch_text.stroke-52"),sQuery(id+"F2.wireOp",EDGE,"E7.sketch_text.stroke-53"),sQuery(id+"F2.wireOp",EDGE,"E7.sketch_text.stroke-54"),sQuery(id+"F2.wireOp",EDGE,"E7.sketch_text.stroke-55"),sQuery(id+"F2.wireOp",EDGE,"E7.sketch_text.stroke-56"),sQuery(id+"F2.wireOp",EDGE,"E7.sketch_text.stroke-57"),sQuery(id+"F2.wireOp",EDGE,"E7.sketch_text.stroke-58"),sQuery(id+"F2.wireOp",EDGE,"E7.sketch_text.stroke-59"),sQuery(id+"F2.wireOp",EDGE,"E7.sketch_text.stroke-60"),sQuery(id+"F2.wireOp",EDGE,"E7.sketch_text.stroke-61"),sQuery(id+"F2.wireOp",EDGE,"E7.sketch_text.stroke-62"),sQuery(id+"F2.wireOp",EDGE,"E7.sketch_text.stroke-63"),sQuery(id+"F2.wireOp",EDGE,"E7.sketch_text.stroke-64"),sQuery(id+"F2.wireOp",EDGE,"E7.sketch_text.stroke-65"),sQuery(id+"F2.wireOp",EDGE,"E7.sketch_text.stroke-66"),sQuery(id+"F2.wireOp",EDGE,"E7.sketch_text.stroke-67"),sQuery(id+"F2.wireOp",EDGE,"E7.sketch_text.stroke-68"),sQuery(id+"F2.wireOp",EDGE,"E7.sketch_text.stroke-69"),sQuery(id+"F2.wireOp",EDGE,"E7.sketch_text.stroke-70"),sQuery(id+"F2.wireOp",EDGE,"E7.sketch_text.stroke-71"),sQuery(id+"F2.wireOp",EDGE,"E7.sketch_text.stroke-72"),sQuery(id+"F2.wireOp",EDGE,"E7.sketch_text.stroke-73"),sQuery(id+"F2.wireOp",EDGE,"E7.sketch_text.stroke-74"),sQuery(id+"F2.wireOp",EDGE,"E7.sketch_text.stroke-75"),sQuery(id+"F2.wireOp",EDGE,"E7.sketch_text.stroke-76"),sQuery(id+"F2.wireOp",EDGE,"E7.sketch_text.stroke-77"),sQuery(id+"F6.wireOp",EDGE,"E20"),sQuery(id+"F9.wireOp",EDGE,"E21.rect.left"),sQuery(id+"F9.wireOp",EDGE,"E21.rect.right"),sQuery(id+"F9.wireOp",EDGE,"E22"),sQuery(id+"F9.wireOp",EDGE,"E23"),sQuery(id+"F9.wireOp",EDGE,"E24"),sQuery(id+"F9.wireOp",EDGE,"E26")])],"isStart":false})});
            var sketch = newSketch(context, id + "F11", { "sketchPlane" : qUnion([Q0])});
            skLineSegment(sketch, "E29.bottom", {"start": v(-35.56, -70.89) * mm, "end": v(30.48, -70.89) * mm});
            skLineSegment(sketch, "E29.top", {"start": v(-35.56, -67.18) * mm, "end": v(30.48, -67.18) * mm});
            skLineSegment(sketch, "E29.left", {"start": v(-35.56, -70.89) * mm, "end": v(-35.56, -67.18) * mm});
            skLineSegment(sketch, "E29.right", {"start": v(30.48, -70.89) * mm, "end": v(30.48, -67.18) * mm});
            skSolve(sketch);
        }
        {
            var Q0;
            Q0=makeQuery(id+"F11.imprint","IMPRINT",FACE,{"disambiguationData":[TD([[makeQuery(id+"F11.imprint","IMPRINT",EDGE,{"derivedFrom":sQuery(id+"F11.wireOp",EDGE,"E29.bottom")}),1.0]])]});
            extrude(context, id + "F12", {"entities" : qUnion([Q0]), "depth" : 2.14 * mm});
        }
        {
            var Q0;
            Q0=makeQuery(id+"F8.opExtrude","CAP_FACE",FACE,{"disambiguationData":[OSD([sQuery(id+"F6.wireOp",EDGE,"E20")])],"isStart":false});
            var sketch = newSketch(context, id + "F13", { "sketchPlane" : qUnion([Q0])});
            skCircle(sketch, "E30", {"center": v(1.55, 3.81) * mm, "radius": 2.6 * mm});
            skSolve(sketch);
        }
        {
            var Q0;
            {var subQ0=sQuery(id+"F2.wireOp",EDGE,"E1.bottom");var subQ1=sQuery(id+"F6.wireOp",EDGE,"E20");var subQ2=makeQuery(id+"F8.opExtrude","CAP_EDGE",EDGE,{"disambiguationData":[OSD([sQuery(id+"F0.wireOp",EDGE,"E0.rect.bottom"),sQuery(id+"F0.wireOp",EDGE,"E0.rect.top"),sQuery(id+"F0.wireOp",EDGE,"E0.rect.left"),sQuery(id+"F0.wireOp",EDGE,"E0.rect.right"),subQ0,subQ1])],"isStart":false});var subQ3=sQuery(id+"F13.wireOp",EDGE,"E30");var subQ4=makeQuery(id+"F13.imprint","INTERSECT",VERTEX,{"derivedFrom":[subQ2,subQ3]});Q0=makeQuery(id+"F13.imprint","IMPRINT",FACE,{"disambiguationData":[TD([[makeQuery(id+"F13.imprint","IMPRINT",EDGE,{"disambiguationData":[TD([[subQ4,-1.0]])],"derivedFrom":subQ3}),1.0]])]});}
            extrude(context, id + "F14", {"entities" : qUnion([Q0]), "operationType" : NewBodyOperationType.ADD, "oppositeDirection" : true, "depth" : 142.08 * mm});
        }
        {
            var Q0;
            Q0=qCreatedBy(makeId("Front.planeOp"),FACE);
            var sketch = newSketch(context, id + "F15", { "sketchPlane" : qUnion([Q0])});
            skLineSegment(sketch, "E31.bottom", {"start": v(-65.04, 10.57) * mm, "end": v(64.5, 10.57) * mm});
            skLineSegment(sketch, "E31.top", {"start": v(-65.04, 5.49) * mm, "end": v(64.5, 5.49) * mm});
            skLineSegment(sketch, "E31.left", {"start": v(-65.04, 10.57) * mm, "end": v(-65.04, 5.49) * mm});
            skLineSegment(sketch, "E31.right", {"start": v(64.5, 10.57) * mm, "end": v(64.5, 5.49) * mm});
            skSolve(sketch);
        }
        {
            var Q0;
            Q0=makeQuery(id+"F15.imprint","IMPRINT",FACE,{"disambiguationData":[TD([[makeQuery(id+"F15.imprint","IMPRINT",EDGE,{"derivedFrom":sQuery(id+"F15.wireOp",EDGE,"E31.bottom")}),-1.0]])]});
            extrude(context, id + "F16", {"entities" : qUnion([Q0]), "depth" : 3.4 * mm});
        }
        {
            var Q0;
            Q0=makeQuery(id+"F16.opExtrude","SWEPT_FACE",FACE,{"disambiguationData":[OSD([sQuery(id+"F15.wireOp",EDGE,"E31.bottom")])]});
            var sketch = newSketch(context, id + "F17", { "sketchPlane" : qUnion([Q0])});
            skLineSegment(sketch, "E32.bottom", {"start": v(-65.04, 0) * mm, "end": v(64.5, 0) * mm});
            skLineSegment(sketch, "E32.top", {"start": v(-65.04, -3.4) * mm, "end": v(64.5, -3.4) * mm});
            skLineSegment(sketch, "E32.left", {"start": v(-65.04, 0) * mm, "end": v(-65.04, -3.4) * mm});
            skLineSegment(sketch, "E32.right", {"start": v(64.5, 0) * mm, "end": v(64.5, -3.4) * mm});
            skSolve(sketch);
        }
        {
            var Q0;
            Q0=makeQuery(id+"F17.imprint","IMPRINT",FACE,{"disambiguationData":[TD([[makeQuery(id+"F17.imprint","IMPRINT",EDGE,{"derivedFrom":sQuery(id+"F17.wireOp",EDGE,"E32.bottom")}),-1.0]])]});
            extrude(context, id + "F18", {"entities" : qUnion([Q0]), "operationType" : NewBodyOperationType.ADD, "depth" : 50.8 * mm});
        }
    });
